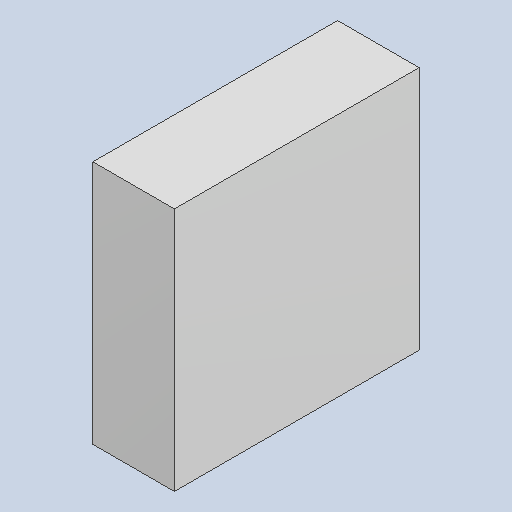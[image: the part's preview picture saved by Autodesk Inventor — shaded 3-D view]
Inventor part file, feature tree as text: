
AUTODESK INVENTOR PART (.ipt)
format: ipt  version: 2023.4 (Build 274418000, 418)  size: 81,408 bytes
history: native  units: mm
features: extrude x1
ambient origin geometry x8: Origin, YZ Plane, XZ Plane, XY Plane, X Axis, Y Axis, Z Axis, Center Point
bodies: Solid1 (feature_tree)
feature tree (1):
  extrude  "Extruded_16"  [1 undecoded]
note: 1 required parameter value undecoded (feature->parameter linkage not recoverable at this tier; creation-order binding heuristic only, values carry confidence <= 0.55)
